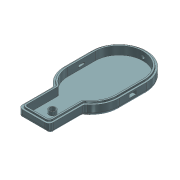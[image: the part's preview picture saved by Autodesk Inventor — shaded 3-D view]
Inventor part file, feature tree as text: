
AUTODESK INVENTOR PART (.ipt)
format: ipt  version: 2022.1 (Build 261234020, 234B)  size: 457,216 bytes
history: native  units: mm
features: extrude x15, sketch x9, fillet x6, other x1, projected_geometry x1
ambient origin geometry x8: Origin, YZ Plane, XZ Plane, XY Plane, X Axis, Y Axis, Z Axis, Center Point
bodies: Solid1 (feature_tree)
feature tree (32):
  sketch  "Sketch1"  dims[d0=70.0mm d1=70.0mm]
  extrude  "Extrusion1"  Depth=70.0mm
  extrude  "Extrusion2"  Depth=80.0mm
  fillet  "Fillet1"  Radius=45.0mm
  extrude  "Extrusion3"  Depth=10.0mm
  sketch  "Sketch3"  dims[d2=40.0mm d3=80.0mm d4=45.0mm]
  extrude  "Extrusion4"  Depth=10.0mm
  extrude  "Extrusion5"  Depth=10.0mm
  extrude  "Extrusion6"  Depth=15.0mm TaperAngle=0.0deg
  extrude  "Extrusion7"  Depth=10.0mm TaperAngle=0.0deg
  sketch  "Sketch5"  dims[d5=10.0mm d6=20.0mm]
  extrude  "Extrusion8"  Depth=10.0mm TaperAngle=0.0deg
  extrude  "Extrusion9"  Depth=5.0mm
  extrude  "Extrusion13"  Depth=10.0mm TaperAngle=0.0deg
  fillet  "Fillet2"  Radius=10.0mm
  fillet  "Fillet4"  Radius=45.0mm
  extrude  "Extrusion14"  Depth=5.0mm
  extrude  "Extrusion15"  Depth=5.0mm TaperAngle=0.0deg
  extrude  "Extrusion16"  Depth=5.0mm TaperAngle=0.0deg
  extrude  "Extrusion17"  Depth=5.0mm
  fillet  "Fillet5"  Radius=17.5mm
  fillet  "Fillet6"  Radius=17.5mm
  fillet  "Fillet7"  Radius=10.0mm
  other  "Lip4"
  extrude  "Extrusion18"  Depth=5.0mm
  sketch  "Sketch9"  dims[d7=40.0mm d8=10.0mm]
  sketch  "Sketch10"  dims[d9=10.0mm d10=20.0mm]
  sketch  "Sketch11"  dims[d11=15.0mm d12=0.0mm d13=15.0mm d14=0.0mm]
  sketch  "Sketch12"  dims[d15=5.0mm d16=10.0mm d17=0.0mm]
  sketch  "Sketch13"  dims[d18=5.0mm d19=10.0mm d20=0.0mm]
  projected_geometry  "Projected Loop2"
  sketch  "Sketch14"  dims[d21=10.0mm d22=0.0mm d23=5.0mm d24=10.0mm d25=0.0mm d26=10.0mm d27=0.0mm d46=45.0mm d47=45.0mm d48=12.5mm d49=0.0mm d50=12.5mm d51=0.0mm d61=5.0mm d62=17.5mm d63=17.5mm d64=10.0mm d65=0.0mm d66=6.0mm d68=3.0mm d69=22.5mm d70=8.0mm d71=10.0mm d72=0.0mm d73=20.0mm d74=5.0mm d75=2.5mm d76=5.0mm d77=5.0mm d78=10.0mm d79=10.0mm d80=0.0mm d81=20.0mm d82=5.0mm d83=20.0mm d84=10.0mm d85=1.3mm d86=1.58mm d87=10.0mm d88=0.0mm d89=5.0mm d90=100.0mm d91=0.0mm d92=5.0mm d93=6.0mm d94=3.0mm d95=2.0mm d96=2.45mm d97=0.0mm d98=0.0mm d99=1.745329mm d100=0.0mm d101=8.1mm d102=10.0mm d103=5.0mm d104=0.0mm d105=80.0mm d106=140.627356mm d107=25.0mm d109=60.0mm]
